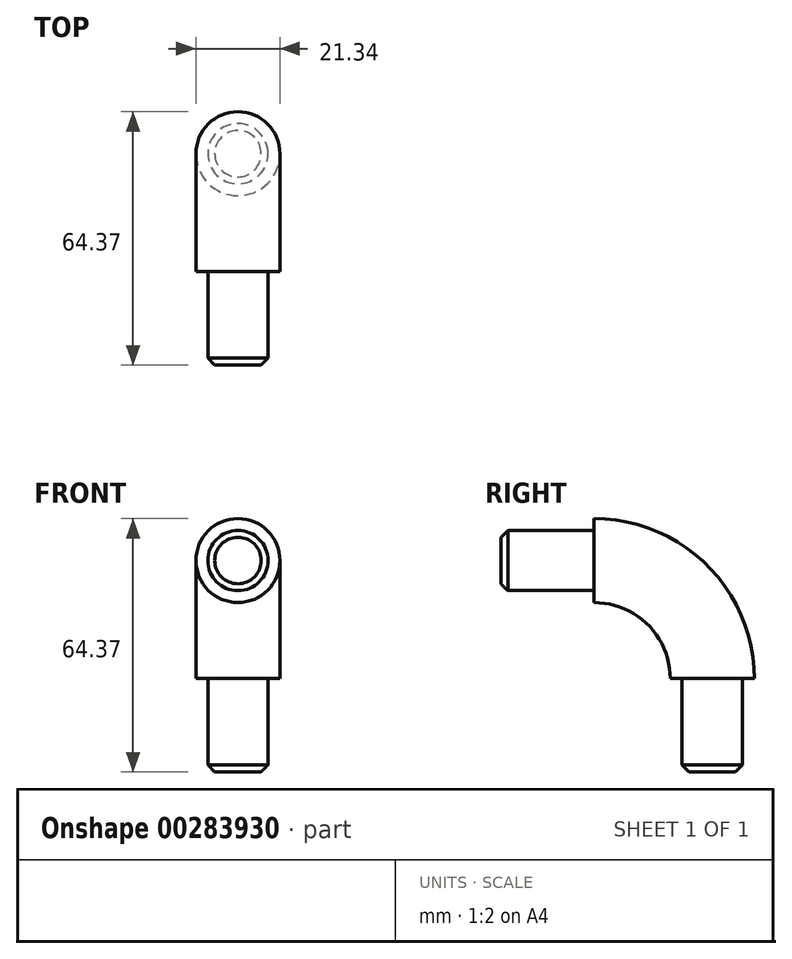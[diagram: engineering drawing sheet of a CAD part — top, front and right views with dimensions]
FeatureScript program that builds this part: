
annotation { "Feature Type Name" : "Feature", "Feature Type Description" : "" }
export const myFeature = defineFeature(function(context is Context, id is Id, definition is map)
    precondition{}
    {
        {
            var Q0;
            Q0=qCreatedBy(makeId("Right.planeOp"),FACE);
            var sketch = newSketch(context, id + "F0", { "sketchPlane" : qUnion([Q0])});
            skArc(sketch, "E0", {"start": v(0, 0) * mm, "mid": v(-8.79, 21.21) * mm, "end": v(-30, 30) * mm});
            skLineSegment(sketch, "E1", {"start": v(-30, 30) * mm, "end": v(-30, 0) * mm, "construction": true});
            skLineSegment(sketch, "E2", {"start": v(0, 0) * mm, "end": v(-30, 0) * mm, "construction": true});
            skPoint(sketch, "E3", {"position": v(-10.67, 0) * mm});
            skSolve(sketch);
        }
        {
            var Q0;
            Q0=qCreatedBy(makeId("Top.planeOp"),FACE);
            var sketch = newSketch(context, id + "F1", { "sketchPlane" : qUnion([Q0])});
            skCircle(sketch, "E4", {"center": v(0, 0) * mm, "radius": 10.67 * mm});
            skCircle(sketch, "E5", {"center": v(0, 0) * mm, "radius": 7.9 * mm, "construction": true});
            skSolve(sketch);
        }
        {
            var Q0;
            Q0 = qSketchRegion(id + "F1", true);
            var Q1;
            Q1=sQuery(id+"F0.wireOp",EDGE,"E0");
            sweep(context, id + "F2", {"profiles" : qUnion([Q0]), "path" : qUnion([Q1])});
        }
        {
            var Q0;
            Q0=makeQuery(id+"F2.opSweep","CAP_FACE",FACE,{"disambiguationData":[OSD([sQuery(id+"F0.wireOp",VERTEX,"E0.start"),sQuery(id+"F1.wireOp",EDGE,"E4")])],"isStart":true});
            var sketch = newSketch(context, id + "F3", { "sketchPlane" : qUnion([Q0])});
            skCircle(sketch, "E6", {"center": v(0, 0) * mm, "radius": 7.9 * mm});
            skSolve(sketch);
        }
        {
            var Q0;
            Q0 = qSketchRegion(id + "F3", true);
            extrude(context, id + "F4", {"entities" : qUnion([Q0]), "operationType" : NewBodyOperationType.ADD, "depth" : 15.8 * mm * 1.5});
        }
        {
            var Q0;
            Q0=makeQuery(id+"F2.opSweep","CAP_FACE",FACE,{"disambiguationData":[OSD([sQuery(id+"F0.wireOp",VERTEX,"E0.end"),sQuery(id+"F1.wireOp",EDGE,"E4")])],"isStart":false});
            var sketch = newSketch(context, id + "F5", { "sketchPlane" : qUnion([Q0])});
            skCircle(sketch, "E7", {"center": v(0, 30) * mm, "radius": 7.9 * mm});
            skSolve(sketch);
        }
        {
            var Q0;
            Q0 = qSketchRegion(id + "F5", true);
            extrude(context, id + "F6", {"entities" : qUnion([Q0]), "operationType" : NewBodyOperationType.ADD, "depth" : 15.8 * mm * 1.5});
        }
        {
            var Q0;
            Q0=makeQuery(id+"F4.opExtrude","CAP_EDGE",EDGE,{"disambiguationData":[OSD([sQuery(id+"F3.wireOp",EDGE,"E6")])],"isStart":false});
            var Q1;
            Q1=makeQuery(id+"F6.opExtrude","CAP_EDGE",EDGE,{"disambiguationData":[OSD([sQuery(id+"F5.wireOp",EDGE,"E7")])],"isStart":false});
            chamfer(context, id + "F7", {"entities" : qUnion([Q0, Q1]), "width" : 2 * mm, "tangentPropagation" : true});
        }
        {
            var Q0;
            Q0=makeQuery(id+"F4.opExtrude","CAP_FACE",FACE,{"disambiguationData":[OSD([sQuery(id+"F3.wireOp",EDGE,"E6")])],"isStart":false});
            var sketch = newSketch(context, id + "F8", { "sketchPlane" : qUnion([Q0])});
            skCircle(sketch, "E8.0", {"center": v(0, 0) * mm, "radius": 7.9 * mm});
            skCircle(sketch, "E9", {"center": v(0, 0) * mm, "radius": 7.65 * mm});
            skSolve(sketch);
        }
        {
            var Q0;
            Q0 = qSketchRegion(id + "F8", true);
            var Q1;
            Q1=makeQuery(id+"F2.opSweep","CAP_FACE",FACE,{"disambiguationData":[OSD([sQuery(id+"F0.wireOp",VERTEX,"E0.start"),sQuery(id+"F1.wireOp",EDGE,"E4")])],"isStart":true});
            extrude(context, id + "F9", {"entities" : qUnion([Q0]), "operationType" : NewBodyOperationType.REMOVE, "endBound" : BoundingType.UP_TO_SURFACE, "oppositeDirection" : true, "endBoundEntityFace" : qUnion([Q1]), "depth" : 25 * mm});
        }
        {
            var Q0;
            Q0=makeQuery(id+"F6.opExtrude","CAP_FACE",FACE,{"disambiguationData":[OSD([sQuery(id+"F5.wireOp",EDGE,"E7")])],"isStart":false});
            var sketch = newSketch(context, id + "F10", { "sketchPlane" : qUnion([Q0])});
            skCircle(sketch, "E10.0", {"center": v(0, 30) * mm, "radius": 7.9 * mm});
            skCircle(sketch, "E11", {"center": v(0, 30) * mm, "radius": 7.65 * mm});
            skSolve(sketch);
        }
        {
            var Q0;
            Q0 = qSketchRegion(id + "F10", true);
            var Q1;
            Q1=makeQuery(id+"F2.opSweep","CAP_FACE",FACE,{"disambiguationData":[OSD([sQuery(id+"F0.wireOp",VERTEX,"E0.end"),sQuery(id+"F1.wireOp",EDGE,"E4")])],"isStart":false});
            extrude(context, id + "F11", {"entities" : qUnion([Q0]), "operationType" : NewBodyOperationType.REMOVE, "endBound" : BoundingType.UP_TO_SURFACE, "oppositeDirection" : true, "endBoundEntityFace" : qUnion([Q1]), "depth" : 25 * mm});
        }
    });
